# Revit family: Door_FTS Wall Slide_The Sliding Door Company_1.5F 2-Panel Bi-part with Single Track (Ramped)
name_source: partatom
category: Doors
units: mm (PartAtom-declared; Revit-internal decimal feet)

## family parameters
Always vertical = Yes
Cut with Voids When Loaded = No
Host = Wall
OmniClass Number = 23.30.10.00
OmniClass Title = Doors
Room Calculation Point = No
Shared = No

## types (1)
- 1.5F 2-Panel Wall Slide - Bi-part - AA
    1 1/2" Frame (No Support Dividers) = Max. H=108 in., Max. W=100 in. (50 in. panel width)
    3" Frame (No Support Dividers) = Max. H=122 in., Max. W=104 in. (52 in. panel width)
    ADA Opening Clearance = 32in. Min. Opening Clearance
    Analytic Construction = <None>
    Configuration = AA Configuration
    Construction Type = Surface Mounted, Ramped Bottom Track
    Description = 2 Panel Wall Slide Bi-part with Single Track (Ramped)
    Finished Opening Height = 96"
    Finished Opening Width = 45"
    Function = Interior
    Glass Thickness = Available in: 5mm Tempered, 7mm,10mm,11mm Laminated Glass
    Height = 98 5/8"
    Limitations = Panel Width x System Height cannot exceed 7,400 square inches
    Manufacturer = The Sliding Door Company
    Model = FTS Wall Slide System - Surface Mounted
    Opening Clearance = 45"
    Order Height = 98 1/8"
    Order Width = 48"
    Overall System Height = 98 5/8"
    Panel Height = 96 3/8"
    Panel Width = 24"
    Rough Height = 98 3/4"
    Rough Width = 49 1/4"
    Stile and Rail = 1 1/2"
    Thickness = 1 1/4"
    Track Length = 97 1/2"
    URL = https://www.slidingdoorco.com
    Wall Closure = By host
    Width = 48"

## geometry (parser evidence)
native form markers: Blend x3, Sweep x12
no freeform markers — native parametric forms only
